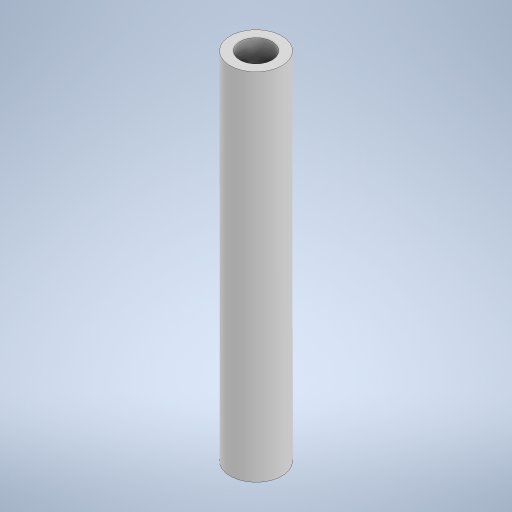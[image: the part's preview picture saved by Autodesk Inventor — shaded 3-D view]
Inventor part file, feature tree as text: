
AUTODESK INVENTOR PART (.ipt)
format: ipt  version: 2024.2 (Build 282272000, 272)  size: 247,808 bytes
history: native  units: mm
features: extrude x3, sketch x3
ambient origin geometry x8: Origin, YZ Plane, XZ Plane, XY Plane, X Axis, Y Axis, Z Axis, Center Point
bodies: Solid1 (feature_tree)
feature tree (6):
  extrude  "Extrusion1"  Depth=5.2mm
  extrude  "Extrusion2"  Depth=5.0mm
  extrude  "Extrusion3"  Depth=50.0mm TaperAngle=0.0deg
  sketch  "Sketch1"  dims[d0=8.0mm d1=5.2mm]
  sketch  "Sketch2"  dims[d2=5.0mm d3=0.0mm d4=3.0mm]
  sketch  "Sketch3"  dims[d5=8.0mm d6=50.0mm d7=0.0mm d8=5.0mm d9=5.0mm d10=0.0mm]
